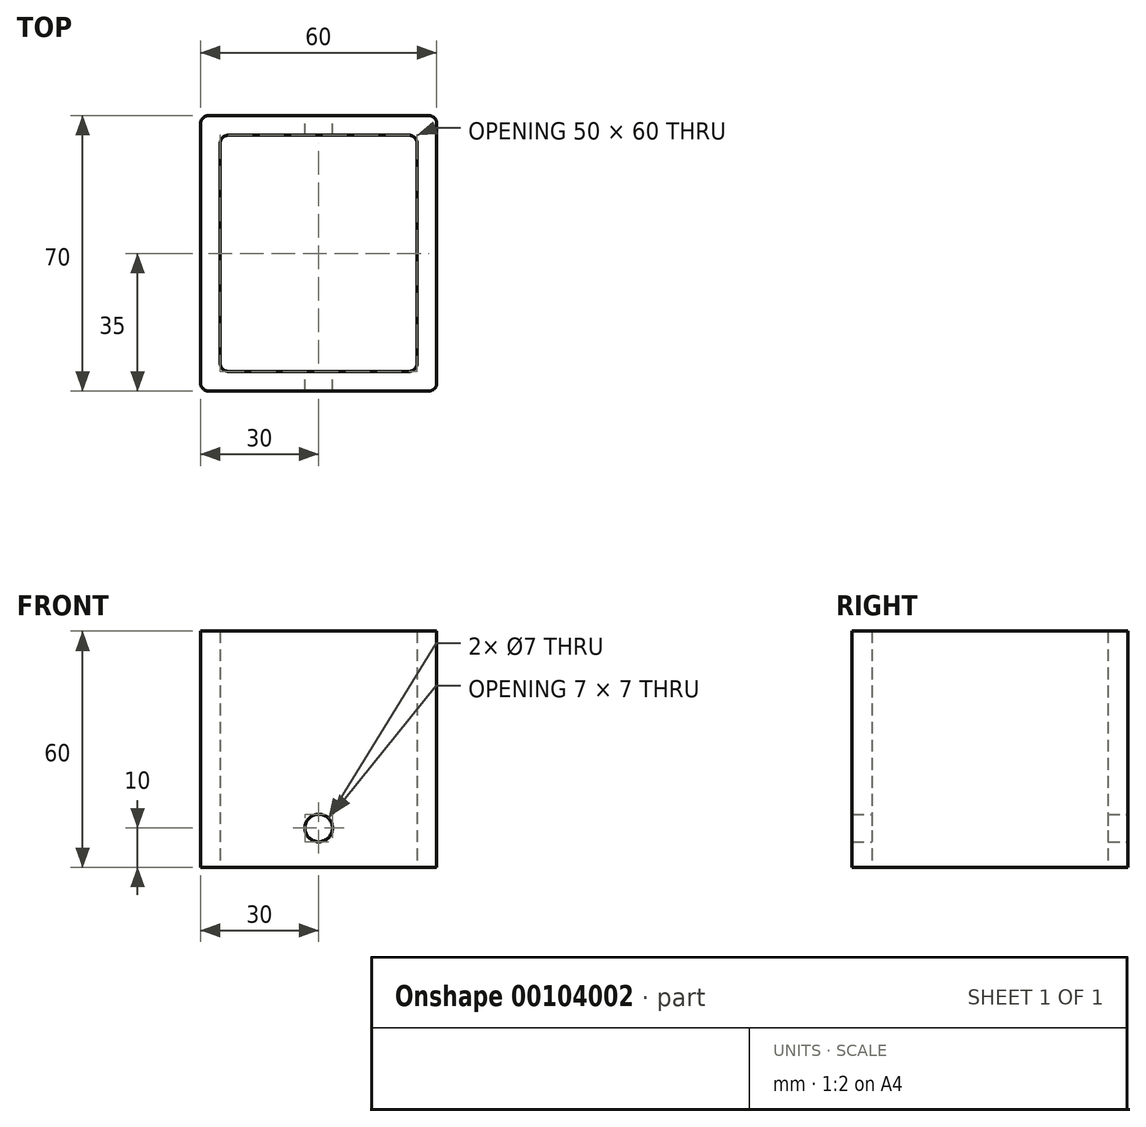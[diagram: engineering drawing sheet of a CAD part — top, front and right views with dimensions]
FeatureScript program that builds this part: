
annotation { "Feature Type Name" : "Feature", "Feature Type Description" : "" }
export const myFeature = defineFeature(function(context is Context, id is Id, definition is map)
    precondition{}
    {
        {
            var Q0;
            Q0=qCreatedBy(makeId("Top.planeOp"),FACE);
            var sketch = newSketch(context, id + "F0", { "sketchPlane" : qUnion([Q0])});
            skLineSegment(sketch, "E0.bottom", {"start": v(-29.9, 25.46) * mm, "end": v(-26.7, 25.46) * mm});
            skLineSegment(sketch, "E0.top", {"start": v(-29.9, 28.64) * mm, "end": v(-26.7, 28.64) * mm});
            skLineSegment(sketch, "E0.left", {"start": v(-29.9, 25.46) * mm, "end": v(-29.9, 28.64) * mm});
            skLineSegment(sketch, "E0.right", {"start": v(-26.7, 25.46) * mm, "end": v(-26.7, 28.64) * mm});
            skPoint(sketch, "E0.middle", {"position": v(-28.3, 27.05) * mm});
            skLineSegment(sketch, "E1.bottom", {"start": v(-30, 35) * mm, "end": v(30, 35) * mm});
            skLineSegment(sketch, "E1.top", {"start": v(-30, -35) * mm, "end": v(30, -35) * mm});
            skLineSegment(sketch, "E1.left", {"start": v(-30, 35) * mm, "end": v(-30, -35) * mm});
            skLineSegment(sketch, "E1.right", {"start": v(30, 35) * mm, "end": v(30, -35) * mm});
            skPoint(sketch, "E1.middle", {"position": v(0, 0) * mm});
            skLineSegment(sketch, "E2.bottom", {"start": v(-25, 30) * mm, "end": v(25, 30) * mm});
            skLineSegment(sketch, "E2.top", {"start": v(-25, -30) * mm, "end": v(25, -30) * mm});
            skLineSegment(sketch, "E2.left", {"start": v(-25, 30) * mm, "end": v(-25, -30) * mm});
            skLineSegment(sketch, "E2.right", {"start": v(25, 30) * mm, "end": v(25, -30) * mm});
            skSolve(sketch);
        }
        {
            var Q0;
            Q0=makeQuery(id+"F0.imprint","IMPRINT",FACE,{"disambiguationData":[TD([[makeQuery(id+"F0.imprint","IMPRINT",EDGE,{"derivedFrom":sQuery(id+"F0.wireOp",EDGE,"E0.bottom")}),1.0]])]});
            var Q1;
            Q1=makeQuery(id+"F0.imprint","IMPRINT",FACE,{"disambiguationData":[TD([[makeQuery(id+"F0.imprint","IMPRINT",EDGE,{"derivedFrom":sQuery(id+"F0.wireOp",EDGE,"E0.bottom")}),-1.0]])]});
            extrude(context, id + "F1", {"entities" : qUnion([Q0, Q1]), "depth" : 60 * mm});
        }
        {
            var Q0;
            Q0=makeQuery(id+"F1.opExtrude","SWEPT_EDGE",EDGE,{"disambiguationData":[OSD([sQuery(id+"F0.wireOp",EDGE,"E1.bottom"),sQuery(id+"F0.wireOp",EDGE,"E1.right")])]});
            var Q1;
            Q1=makeQuery(id+"F1.opExtrude","SWEPT_EDGE",EDGE,{"disambiguationData":[OSD([sQuery(id+"F0.wireOp",EDGE,"E1.top"),sQuery(id+"F0.wireOp",EDGE,"E1.right")])]});
            var Q2;
            Q2=makeQuery(id+"F1.opExtrude","SWEPT_EDGE",EDGE,{"disambiguationData":[OSD([sQuery(id+"F0.wireOp",EDGE,"E1.bottom"),sQuery(id+"F0.wireOp",EDGE,"E1.left")])]});
            var Q3;
            Q3=makeQuery(id+"F1.opExtrude","SWEPT_EDGE",EDGE,{"disambiguationData":[OSD([sQuery(id+"F0.wireOp",EDGE,"E1.top"),sQuery(id+"F0.wireOp",EDGE,"E1.left")])]});
            fillet(context, id + "F2", {"entities" : qUnion([Q0, Q1, Q2, Q3]), "radius" : 2 * mm, "tangentPropagation" : true, "allowEdgeOverflow" : false});
        }
        {
            var Q0;
            Q0=makeQuery(id+"F1.opExtrude","SWEPT_EDGE",EDGE,{"disambiguationData":[OSD([sQuery(id+"F0.wireOp",EDGE,"E2.bottom"),sQuery(id+"F0.wireOp",EDGE,"E2.left")])]});
            var Q1;
            Q1=makeQuery(id+"F1.opExtrude","SWEPT_EDGE",EDGE,{"disambiguationData":[OSD([sQuery(id+"F0.wireOp",EDGE,"E2.top"),sQuery(id+"F0.wireOp",EDGE,"E2.right")])]});
            var Q2;
            Q2=makeQuery(id+"F1.opExtrude","SWEPT_EDGE",EDGE,{"disambiguationData":[OSD([sQuery(id+"F0.wireOp",EDGE,"E2.bottom"),sQuery(id+"F0.wireOp",EDGE,"E2.right")])]});
            var Q3;
            Q3=makeQuery(id+"F1.opExtrude","SWEPT_EDGE",EDGE,{"disambiguationData":[OSD([sQuery(id+"F0.wireOp",EDGE,"E2.top"),sQuery(id+"F0.wireOp",EDGE,"E2.left")])]});
            fillet(context, id + "F3", {"entities" : qUnion([Q0, Q1, Q2, Q3]), "radius" : 2 * mm, "tangentPropagation" : true, "allowEdgeOverflow" : false});
        }
        {
            var Q0;
            Q0=qCreatedBy(makeId("Front.planeOp"),FACE);
            var sketch = newSketch(context, id + "F4", { "sketchPlane" : qUnion([Q0])});
            skCircle(sketch, "E3", {"center": v(0, 10) * mm, "radius": 3.5 * mm});
            skSolve(sketch);
        }
        {
            var Q0;
            Q0=makeQuery(id+"F4.imprint","IMPRINT",FACE,{"disambiguationData":[TD([[makeQuery(id+"F4.imprint","IMPRINT",EDGE,{"derivedFrom":sQuery(id+"F4.wireOp",EDGE,"E3")}),1.0]])]});
            extrude(context, id + "F5", {"entities" : qUnion([Q0]), "operationType" : NewBodyOperationType.REMOVE, "endBound" : BoundingType.SYMMETRIC, "depth" : 70 * mm});
        }
    });
